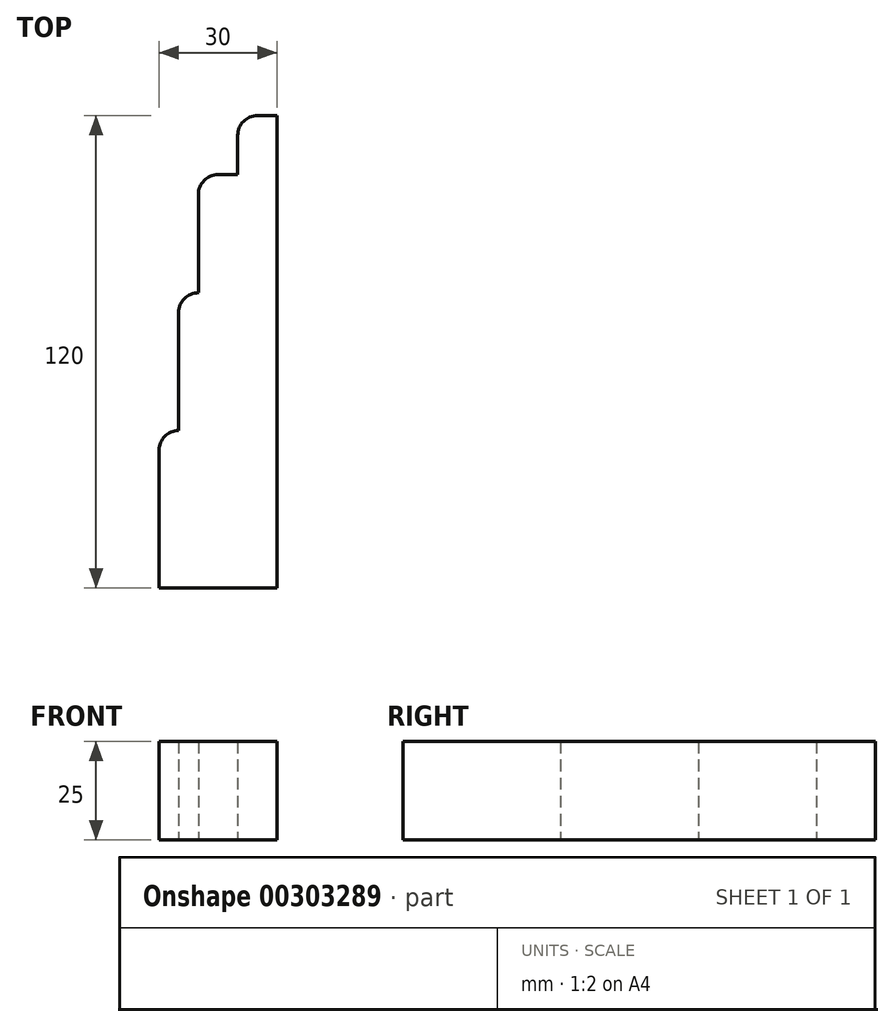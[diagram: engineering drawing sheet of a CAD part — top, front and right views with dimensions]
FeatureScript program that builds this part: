
annotation { "Feature Type Name" : "Feature", "Feature Type Description" : "" }
export const myFeature = defineFeature(function(context is Context, id is Id, definition is map)
    precondition{}
    {
        {
            var Q0;
            Q0=qCreatedBy(makeId("Top.planeOp"),FACE);
            var sketch = newSketch(context, id + "F0", { "sketchPlane" : qUnion([Q0])});
            skLineSegment(sketch, "E0", {"start": v(41.45, 69.09) * mm, "end": v(41.45, -50.91) * mm});
            skLineSegment(sketch, "E1", {"start": v(41.45, -50.91) * mm, "end": v(11.45, -50.91) * mm});
            skLineSegment(sketch, "E2", {"start": v(11.45, -50.91) * mm, "end": v(11.45, -15.91) * mm});
            skLineSegment(sketch, "E3", {"start": v(16.45, -10.91) * mm, "end": v(16.45, -10.91) * mm});
            skLineSegment(sketch, "E4", {"start": v(16.45, -10.91) * mm, "end": v(16.45, 19.09) * mm});
            skLineSegment(sketch, "E5", {"start": v(21.45, 24.09) * mm, "end": v(21.45, 24.09) * mm});
            skLineSegment(sketch, "E6", {"start": v(21.45, 24.09) * mm, "end": v(21.45, 49.09) * mm});
            skLineSegment(sketch, "E7", {"start": v(26.45, 54.09) * mm, "end": v(31.45, 54.09) * mm});
            skLineSegment(sketch, "E8", {"start": v(31.45, 54.09) * mm, "end": v(31.45, 64.09) * mm});
            skLineSegment(sketch, "E9", {"start": v(36.45, 69.09) * mm, "end": v(41.45, 69.09) * mm});
            skPoint(sketch, "E10.visualSharp", {"position": v(21.45, 54.09) * mm});
            skArc(sketch, "E10.filletArc", {"start": v(26.45, 54.09) * mm, "mid": v(22.91, 52.62) * mm, "end": v(21.45, 49.09) * mm});
            skPoint(sketch, "E11.visualSharp", {"position": v(31.45, 69.09) * mm});
            skArc(sketch, "E11.filletArc", {"start": v(36.45, 69.09) * mm, "mid": v(32.91, 67.62) * mm, "end": v(31.45, 64.09) * mm});
            skPoint(sketch, "E12.visualSharp", {"position": v(16.45, 24.09) * mm});
            skArc(sketch, "E12.filletArc", {"start": v(21.45, 24.09) * mm, "mid": v(17.91, 22.62) * mm, "end": v(16.45, 19.09) * mm});
            skPoint(sketch, "E13.visualSharp", {"position": v(11.45, -10.91) * mm});
            skArc(sketch, "E13.filletArc", {"start": v(16.45, -10.91) * mm, "mid": v(12.91, -12.38) * mm, "end": v(11.45, -15.91) * mm});
            skSolve(sketch);
        }
        {
            var Q0;
            Q0=makeQuery(id+"F0.imprint","IMPRINT",FACE,{"disambiguationData":[TD([[makeQuery(id+"F0.imprint","IMPRINT",EDGE,{"derivedFrom":sQuery(id+"F0.wireOp",EDGE,"E0")}),-1.0]])]});
            extrude(context, id + "F1", {"entities" : qUnion([Q0]), "depth" : 25 * mm});
        }
    });
